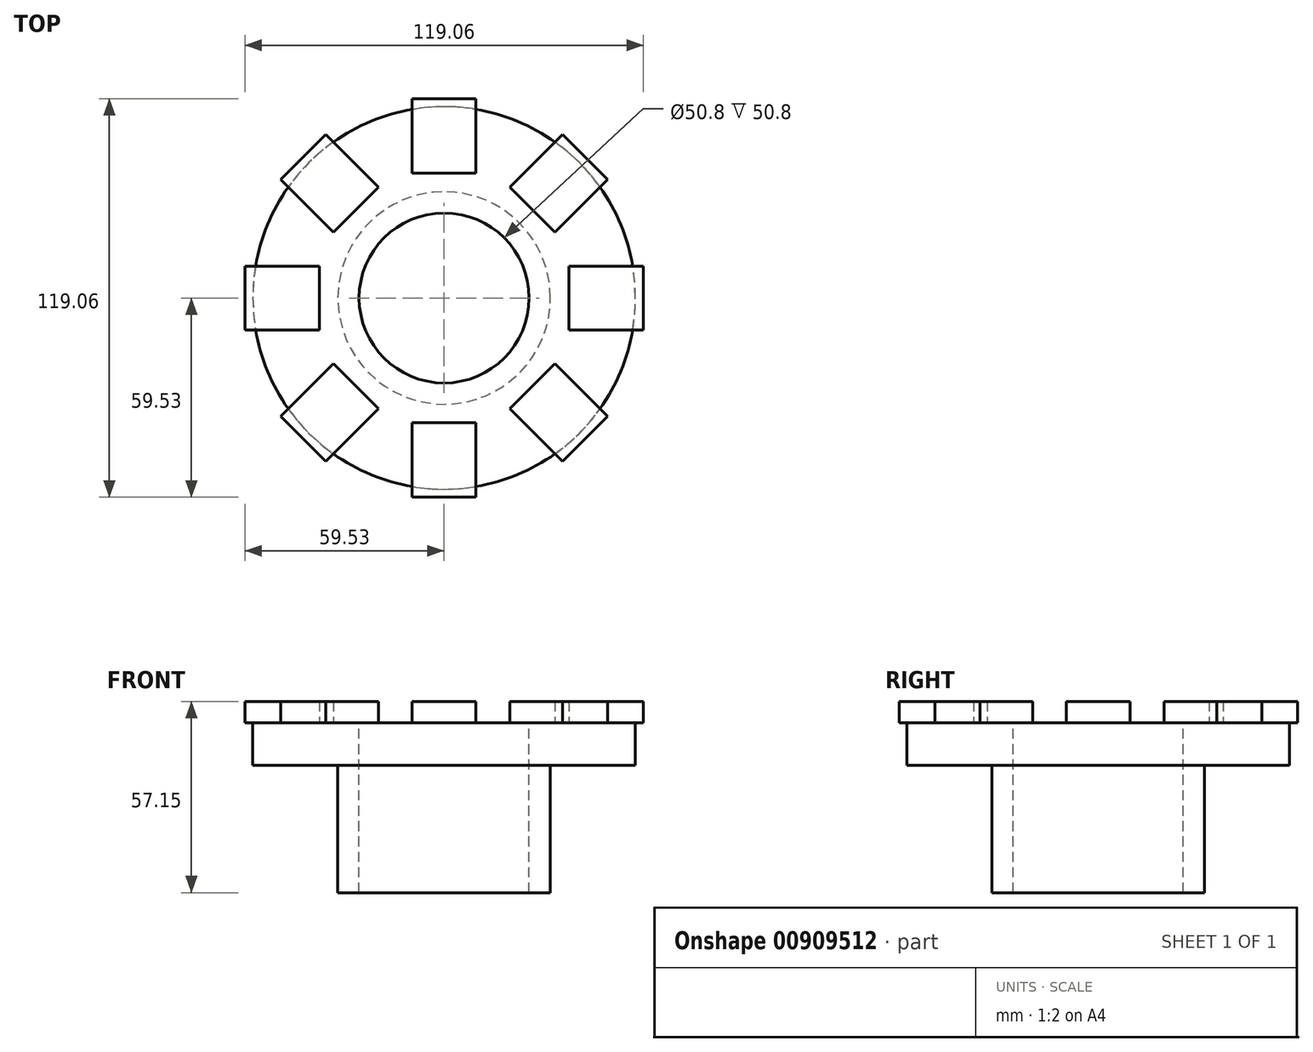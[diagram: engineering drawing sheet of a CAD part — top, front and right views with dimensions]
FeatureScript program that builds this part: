
annotation { "Feature Type Name" : "Feature", "Feature Type Description" : "" }
export const myFeature = defineFeature(function(context is Context, id is Id, definition is map)
    precondition{}
    {
        {
            var Q0;
            Q0=qCreatedBy(makeId("Front.planeOp"),FACE);
            var sketch = newSketch(context, id + "F0", { "sketchPlane" : qUnion([Q0])});
            skLineSegment(sketch, "E0", {"start": v(25.4, -50.8) * mm, "end": v(31.75, -50.8) * mm});
            skLineSegment(sketch, "E1", {"start": v(31.75, -50.8) * mm, "end": v(31.75, -12.7) * mm});
            skLineSegment(sketch, "E2", {"start": v(31.75, -12.7) * mm, "end": v(57.15, -12.7) * mm});
            skLineSegment(sketch, "E3", {"start": v(57.15, -12.7) * mm, "end": v(57.15, 0) * mm});
            skLineSegment(sketch, "E4", {"start": v(57.15, 0) * mm, "end": v(25.4, 0) * mm});
            skLineSegment(sketch, "E5", {"start": v(25.4, 0) * mm, "end": v(25.4, -50.8) * mm});
            skLineSegment(sketch, "E6", {"start": v(0, 40.65) * mm, "end": v(0, -35.3) * mm});
            skSolve(sketch);
        }
        {
            var Q0;
            Q0=makeQuery(id+"F0.imprint","IMPRINT",FACE,{"disambiguationData":[TD([[makeQuery(id+"F0.imprint","IMPRINT",EDGE,{"derivedFrom":sQuery(id+"F0.wireOp",EDGE,"E0")}),1.0]])]});
            var Q1;
            Q1=sQuery(id+"F0.wireOp",EDGE,"E6");
            revolve(context, id + "F1", {"surfaceOperationType" : NewSurfaceOperationType.NEW, "entities" : qUnion([Q0]), "axis" : qUnion([Q1]), "revolveType" : RevolveType.FULL});
        }
        {
            var Q0;
            Q0=makeQuery(id+"F1.opRevolve","SWEPT_FACE",FACE,{"disambiguationData":[OSD([sQuery(id+"F0.wireOp",EDGE,"E4")])]});
            var sketch = newSketch(context, id + "F2", { "sketchPlane" : qUnion([Q0])});
            skLineSegment(sketch, "E7.top", {"start": v(37.3, -9.53) * mm, "end": v(59.53, -9.53) * mm});
            skLineSegment(sketch, "E7.left", {"start": v(37.3, 9.53) * mm, "end": v(37.3, -9.53) * mm});
            skLineSegment(sketch, "E7.right", {"start": v(59.53, 9.52) * mm, "end": v(59.53, -9.53) * mm});
            skLineSegment(sketch, "E8", {"start": v(37.3, 9.53) * mm, "end": v(56.35, 9.53) * mm});
            skLineSegment(sketch, "E9", {"start": v(56.35, 9.53) * mm, "end": v(59.53, 9.53) * mm});
            skSolve(sketch);
        }
        {
            var Q0;
            Q0=qCreatedBy(makeId("Right.planeOp"),FACE);
            var sketch = newSketch(context, id + "F3", { "sketchPlane" : qUnion([Q0])});
            skLineSegment(sketch, "E10", {"start": v(0, 0) * mm, "end": v(0, 44.55) * mm});
            skSolve(sketch);
        }
        {
            var Q0;
            {var subQ0=sQuery(id+"F2.wireOp",EDGE,"5LIAd6Vz-sC3Z-bJuG-omaF-mCK6PUYyLqyZ.bottom");Q0=makeQuery(id+"F2.imprint","IMPRINT",FACE,{"disambiguationData":[TD([[makeQuery(id+"F2.imprint","IMPRINT",EDGE,{"derivedFrom":subQ0}),-1.0]])]});}
            var Q1;
            {var subQ0=sQuery(id+"F2.wireOp",EDGE,"uaLS89qE-0Pks-rpu5-r1hJ-BHvm0EwHUPRP.bottom");Q1=makeQuery(id+"F2.imprint","IMPRINT",FACE,{"disambiguationData":[TD([[makeQuery(id+"F2.imprint","IMPRINT",EDGE,{"derivedFrom":subQ0}),-1.0]])]});}
            var Q2;
            {var subQ0=sQuery(id+"F2.wireOp",EDGE,"E7.right");Q2=makeQuery(id+"F2.imprint","IMPRINT",FACE,{"disambiguationData":[TD([[makeQuery(id+"F2.imprint","IMPRINT",EDGE,{"derivedFrom":subQ0}),-1.0]])]});}
            var Q3;
            {var subQ0=sQuery(id+"F2.wireOp",EDGE,"E7.left");Q3=makeQuery(id+"F2.imprint","IMPRINT",FACE,{"disambiguationData":[TD([[makeQuery(id+"F2.imprint","IMPRINT",EDGE,{"derivedFrom":subQ0}),1.0]])]});}
            extrude(context, id + "F4", {"entities" : qUnion([Q0, Q1, Q2, Q3]), "operationType" : NewBodyOperationType.ADD, "depth" : 6.35 * mm, "offsetDistance" : 25.4 * mm});
        }
        {
            var Q0;
            Q0=makeQuery(id+"F1.opRevolve","SWEPT_BODY",BODY,{"disambiguationData":[OSD([sQuery(id+"F0.wireOp",EDGE,"E0"),sQuery(id+"F0.wireOp",EDGE,"E1"),sQuery(id+"F0.wireOp",EDGE,"E2"),sQuery(id+"F0.wireOp",EDGE,"E3"),sQuery(id+"F0.wireOp",EDGE,"E4"),sQuery(id+"F0.wireOp",EDGE,"E5")])]});
            var Q1;
            Q1=sQuery(id+"F3.wireOp",EDGE,"E10");
            circularPattern(context, id + "F5", {"operationType" : NewBodyOperationType.ADD, "entities" : qUnion([Q0]), "axis" : qUnion([Q1]), "angle" : 360 * degree, "instanceCount" : 8, "equalSpace" : true, "isCentered" : true});
        }
    });
